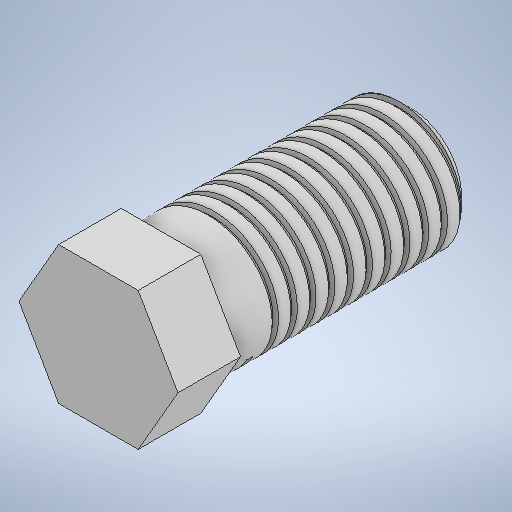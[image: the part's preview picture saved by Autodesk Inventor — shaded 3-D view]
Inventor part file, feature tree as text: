
AUTODESK INVENTOR PART (.ipt)
format: ipt  version: 2025.2 (Build 292293000, 293)  size: 476,672 bytes
history: native  units: mm
features: sketch x3, other x2, extrude x2, chamfer x1
ambient origin geometry x8: Origin, YZ Plane, XZ Plane, XY Plane, X Axis, Y Axis, Z Axis, Center Point
bodies: Body1 (feature_tree)
feature tree (8):
  other  "Sólido1"
  extrude  "Extrusão1"  Depth=20.0mm TaperAngle=0.0deg
  other  "Espiral1"
  chamfer  "Chanfro1"  Distance=11.0mm
  extrude  "Extrusão2"  Depth=10.0mm TaperAngle=0.0deg
  sketch  "Esboço1"  dims[d0=20.0mm d1=40.0mm d2=0.0mm]
  sketch  "Esboço2"  dims[d6=1.0mm]
  sketch  "Esboço5"  dims[d7=0.2mm d8=3.0mm d9=35.0mm d10=10.0mm d11=0.0mm d12=90.0deg d13=90.0deg d14=0.0mm d15=0.0mm d16=2.0mm d17=2.0mm d18=45.0deg d20=11.0mm d21=10.0mm d22=0.0mm d24=0.5mm d25=0.872665mm d26=0.5mm d27=0.872665mm]
